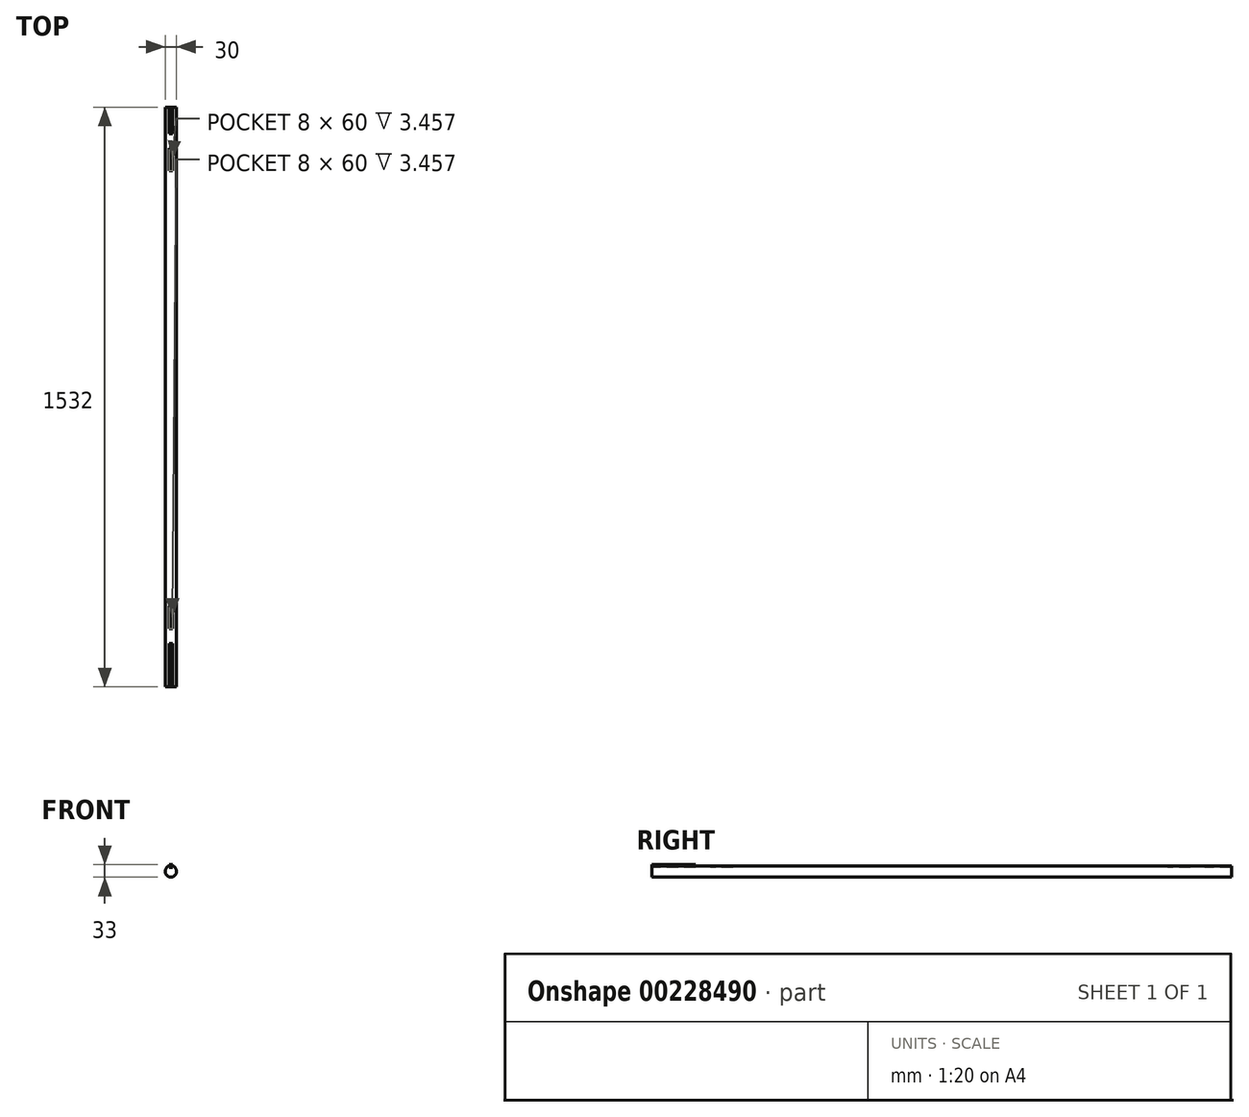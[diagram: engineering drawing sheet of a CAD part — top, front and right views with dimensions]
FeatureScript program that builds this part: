
annotation { "Feature Type Name" : "Feature", "Feature Type Description" : "" }
export const myFeature = defineFeature(function(context is Context, id is Id, definition is map)
    precondition{}
    {
        {
            var Q0;
            Q0=qCreatedBy(makeId("Front.planeOp"),FACE);
            var sketch = newSketch(context, id + "F0", { "sketchPlane" : qUnion([Q0])});
            skCircle(sketch, "E0", {"center": v(0, 0) * mm, "radius": 15 * mm});
            skSolve(sketch);
        }
        {
            var Q0;
            Q0=qSketchRegion(id+"F0",true);
            extrude(context, id + "F1", {"entities" : qUnion([Q0]), "depth" : 1532 * mm, "offsetDistance" : 25 * mm, "symmetric" : true});
        }
        {
            var Q0;
            Q0=qCreatedBy(makeId("Top.planeOp"),FACE);
            cPlane(context, id + "F2", {"entities" : qUnion([Q0]), "cplaneType" : CPlaneType.OFFSET, "offset" : 15 * mm, "width" : 150 * mm, "height" : 150 * mm});
        }
        {
            var Q0;
            Q0=qCreatedBy(id+"F2.planeOp",FACE);
            var sketch = newSketch(context, id + "F3", { "sketchPlane" : qUnion([Q0])});
            skLineSegment(sketch, "E1.bottom", {"start": v(-4, 766) * mm, "end": v(4, 766) * mm});
            skLineSegment(sketch, "E1.top", {"start": v(-4, 696) * mm, "end": v(4, 696) * mm});
            skLineSegment(sketch, "E1.left", {"start": v(-4, 766) * mm, "end": v(-4, 696) * mm});
            skLineSegment(sketch, "E1.right", {"start": v(4, 766) * mm, "end": v(4, 696) * mm});
            skLineSegment(sketch, "E2.bottom", {"start": v(-4, -552) * mm, "end": v(4, -552) * mm});
            skLineSegment(sketch, "E2.top", {"start": v(-4, -612) * mm, "end": v(4, -612) * mm});
            skLineSegment(sketch, "E2.left", {"start": v(-4, -552) * mm, "end": v(-4, -612) * mm});
            skLineSegment(sketch, "E2.right", {"start": v(4, -552) * mm, "end": v(4, -612) * mm});
            skLineSegment(sketch, "E3.bottom", {"start": v(-4, -651) * mm, "end": v(4, -651) * mm});
            skLineSegment(sketch, "E3.top", {"start": v(-4, -766) * mm, "end": v(4, -766) * mm});
            skLineSegment(sketch, "E3.left", {"start": v(-4, -651) * mm, "end": v(-4, -766) * mm});
            skLineSegment(sketch, "E3.right", {"start": v(4, -651) * mm, "end": v(4, -766) * mm});
            skLineSegment(sketch, "E4.bottom", {"start": v(-4, 658) * mm, "end": v(4, 658) * mm});
            skLineSegment(sketch, "E4.top", {"start": v(-4, 598) * mm, "end": v(4, 598) * mm});
            skLineSegment(sketch, "E4.left", {"start": v(-4, 658) * mm, "end": v(-4, 598) * mm});
            skLineSegment(sketch, "E4.right", {"start": v(4, 658) * mm, "end": v(4, 598) * mm});
            skSolve(sketch);
        }
        {
            var Q0;
            Q0=qSketchRegion(id+"F3",true);
            extrude(context, id + "F4", {"entities" : qUnion([Q0]), "operationType" : NewBodyOperationType.REMOVE, "oppositeDirection" : true, "depth" : 4 * mm, "offsetDistance" : 25 * mm});
        }
        {
            var Q0;
            Q0=makeQuery(id+"F4.boolean.opBoolean","COPY",FACE,{"derivedFrom":makeQuery(id+"F4.opExtrude","CAP_FACE",FACE,{"disambiguationData":[OSD([sQuery(id+"F3.wireOp",EDGE,"E3.bottom"),sQuery(id+"F3.wireOp",EDGE,"E3.top"),sQuery(id+"F3.wireOp",EDGE,"E3.left"),sQuery(id+"F3.wireOp",EDGE,"E3.right")])],"isStart":false})});
            extrude(context, id + "F5", {"entities" : qUnion([Q0]), "depth" : 7 * mm, "offsetDistance" : 25 * mm});
        }
    });
